# Revit family: Gleitschlitten Typ HV1, o.D., Ø219 - Ø508mm, (h=94-150 mm)
name_source: partatom
category: HLS-Bauteile
units: mm (PartAtom-declared; Revit-internal decimal feet)

## family parameters
Arbeitsebenenbasiert = Ja
Beim Laden mit Abzugskörper schneiden = Nein
Bemaßung runder Anschluss = Durchmesser verwenden
Beschriftungsausrichtung beibehalten = Nein
Gemeinsam genutzt = Ja
Immer vertikal = Nein
Klassifizierung = Keine
Raumberechnungspunkt = Nein
Teiletyp = Normal

## types (13) — shared parameters
Breite Schellenband = 50 mm
Fabrikat = MEFA
Kurztext1 = Gleitschlitten A HV 100-150 50x5
Material = Stahl
Materialname = S235
Mengeneinheit = St
Schalldämmeinlage = ohne Dämmung
Sicherheitsfaktor = 1.54
Stärke Schellenband = 5 mm
Verschluss = Mutter / Verschluss-Schraube
Verschluss-Schraube = M12
Vorgabe-Ansicht = 1219 mm
max. Höhe Unterbau = 150 mm
min. Höhe Unterbau = 100 mm
vpe = 1
zero-valued in all types: Dämmstärke

## per-type parameters (varying)
| type | A (Breite) | Achse Bohrloch | Artikelnummer | Breite Unterbau | EAN | Gewicht | Gewicht pro Bauteil | Kurztext2 | L | L Unterbau | Länge Unterbau | Nennweite DN Rohr | Rohraußendurchmesser | Schellenteil | Stärke Material | TL-Fuß |
| Gleitschlitten HV1, o.D., Ø219mm, h=94mm bis h=150mm | 140 mm  [stored 0.459318 ft] | 90 mm  [stored 0.295276 ft] | 142afa0219 | 256 mm | 4250928462534 | 11.95 kg | 11.95 kg | 219 mm o. Dämm. fsv | 160 mm  [stored 0.524934 ft] | 270 mm  [stored 0.885827 ft] | 270 mm | 200 mm  [stored 0.656168 ft] | 219 mm  [stored 0.718504 ft] | Schellenteil für HV mit RS oD : Schellenteil für 219 | 6 mm  [stored 0.019685 ft] | Gruppe Gleischlitten HV1 Ø219 bis 508 : Gl.0219 |
| Gleitschlitten HV1, o.D., Ø225mm, h=94mm bis h=150mm | 140 mm  [stored 0.459318 ft] | 90 mm  [stored 0.295276 ft] | 142afa0225 | 256 mm | 4250928462541 | 12.12 kg | 12.12 kg | 225 mm o. Dämm. fsv | 160 mm  [stored 0.524934 ft] | 270 mm  [stored 0.885827 ft] | 270 mm | 0 mm  [stored 0 ft] | 225 mm  [stored 0.738189 ft] | Schellenteil für HV mit RS oD : Schellenteil für 225 | 6 mm  [stored 0.019685 ft] | Gruppe Gleischlitten HV1 Ø219 bis 508 : Gl.0225 |
| Gleitschlitten HV1, o.D., Ø273mm, h=94mm bis h=150mm | 172 mm  [stored 0.564304 ft] | 90 mm  [stored 0.295276 ft] | 142afa0273 | 288 mm | 4250928462558 | 12.99 kg | 12.99 kg | 273 mm o. Dämm. fsv | 160 mm  [stored 0.524934 ft] | 270 mm  [stored 0.885827 ft] | 270 mm | 250 mm  [stored 0.82021 ft] | 273 mm  [stored 0.895669 ft] | Schellenteil für HV mit RS oD : Schellenteil für 273 | 6 mm  [stored 0.019685 ft] | Gruppe Gleischlitten HV1 Ø219 bis 508 : Gl.0273 |
| Gleitschlitten HV1, o.D., Ø280mm, h=94mm bis h=150mm | 172 mm  [stored 0.564304 ft] | 90 mm  [stored 0.295276 ft] | 142afa0280 | 288 mm | 4250928462565 | 13.08 kg | 13.08 kg | 280 mm o. Dämm. fsv | 160 mm  [stored 0.524934 ft] | 270 mm  [stored 0.885827 ft] | 270 mm | 0 mm  [stored 0 ft] | 280 mm  [stored 0.918635 ft] | Schellenteil für HV mit RS oD : Schellenteil für 280 | 6 mm  [stored 0.019685 ft] | Gruppe Gleischlitten HV1 Ø219 bis 508 : Gl.0280 |
| Gleitschlitten HV1, o.D., Ø315mm, h=94mm bis h=150mm | 172 mm  [stored 0.564304 ft] | 90 mm  [stored 0.295276 ft] | 142afa0315 | 288 mm | 4250928462572 | 13.43 kg | 13.43 kg | 315 mm o. Dämm. fsv | 160 mm  [stored 0.524934 ft] | 270 mm  [stored 0.885827 ft] | 270 mm | 0 mm  [stored 0 ft] | 315 mm  [stored 1.03346 ft] | Schellenteil für HV mit RS oD : Schellenteil für 315 | 6 mm  [stored 0.019685 ft] | Gruppe Gleischlitten HV1 Ø219 bis 508 : Gl.0315 |
| Gleitschlitten HV1, o.D., Ø324mm, h=94mm bis h=150mm | 172 mm  [stored 0.564304 ft] | 90 mm  [stored 0.295276 ft] | 142afa0324 | 288 mm | 4250928462589 | 13.56 kg | 13.56 kg | 324 mm o. Dämm. fsv | 160 mm  [stored 0.524934 ft] | 270 mm  [stored 0.885827 ft] | 270 mm | 300 mm | 324 mm  [stored 1.06299 ft] | Schellenteil für HV mit RS oD : Schellenteil für 324 | 6 mm  [stored 0.019685 ft] | Gruppe Gleischlitten HV1 Ø219 bis 508 : Gl.0324 |
| Gleitschlitten HV1, o.D., Ø356mm, h=94mm bis h=150mm | 172 mm  [stored 0.564304 ft] | 90 mm  [stored 0.295276 ft] | 142afa0356 | 288 mm | 4250928462596 | 13.87 kg | 13.87 kg | 356 mm o. Dämm. fsv | 160 mm  [stored 0.524934 ft] | 270 mm  [stored 0.885827 ft] | 270 mm | 0 mm  [stored 0 ft] | 356 mm  [stored 1.16798 ft] | Schellenteil für HV mit RS oD : Schellenteil für 356 | 6 mm  [stored 0.019685 ft] | Gruppe Gleischlitten HV1 Ø219 bis 508 : Gl.0356 |
| Gleitschlitten HV1, o.D., Ø400mm, h=94mm bis h=150mm | 225 mm  [stored 0.738189 ft] | 95 mm  [stored 0.31168 ft] | 142afa0400 | 341 mm | 4250928462602 | 17.57 kg | 17.57 kg | 400 mm o. Dämm. fsv | 160 mm  [stored 0.524934 ft] | 270 mm  [stored 0.885827 ft] | 270 mm | 0 mm  [stored 0 ft] | 400 mm  [stored 1.31234 ft] | Schellenteil für HV mit RS oD : Schellenteil für 400 | 8 mm  [stored 0.0262467 ft] | Gruppe Gleischlitten HV1 Ø219 bis 508 : Gl.0400 |
| Gleitschlitten HV1, o.D., Ø406mm, h=94mm bis h=150mm | 225 mm  [stored 0.738189 ft] | 95 mm  [stored 0.31168 ft] | 142afa0406 | 341 mm | 4250928462619 | 17.70 kg | 17.70 kg | 406 mm o. Dämm. fsv | 160 mm  [stored 0.524934 ft] | 270 mm  [stored 0.885827 ft] | 270 mm | 400 mm  [stored 1.31234 ft] | 406 mm  [stored 1.33202 ft] | Schellenteil für HV mit RS oD : Schellenteil für 406 | 8 mm  [stored 0.0262467 ft] | Gruppe Gleischlitten HV1 Ø219 bis 508 : Gl.0406 |
| Gleitschlitten HV1, o.D., Ø450mm, h=94mm bis h=150mm | 225 mm  [stored 0.738189 ft] | 95 mm  [stored 0.31168 ft] | 142afa0450 | 341 mm | 4250928462626 | 18.24 kg | 18.24 kg | 450 mm o. Dämm. fsv | 160 mm  [stored 0.524934 ft] | 270 mm  [stored 0.885827 ft] | 270 mm | 0 mm  [stored 0 ft] | 450 mm  [stored 1.47638 ft] | Schellenteil für HV mit RS oD : Schellenteil für 450 | 8 mm  [stored 0.0262467 ft] | Gruppe Gleischlitten HV1 Ø219 bis 508 : Gl.0450 |
| Gleitschlitten HV1, o.D., Ø457mm, h=94mm bis h=150mm | 225 mm  [stored 0.738189 ft] | 95 mm  [stored 0.31168 ft] | 142afa0457 | 341 mm | 4250928462633 | 18.17 kg | 18.17 kg | 457 mm o. Dämm. fsv | 160 mm  [stored 0.524934 ft] | 270 mm  [stored 0.885827 ft] | 270 mm | 450 mm  [stored 1.47638 ft] | 457 mm  [stored 1.49934 ft] | Schellenteil für HV mit RS oD : Schellenteil für 457 | 8 mm  [stored 0.0262467 ft] | Gruppe Gleischlitten HV1 Ø219 bis 508 : Gl.0457 |
| Gleitschlitten HV1, o.D., Ø500mm, h=94mm bis h=150mm | 254 mm  [stored 0.833333 ft] | 100 mm  [stored 0.328084 ft] | 142afa0500 | 370 mm | 4250928462640 | 24.44 kg | 24.44 kg | 500 mm o. Dämm. fsv | 280 mm  [stored 0.918635 ft] | 390 mm  [stored 1.27953 ft] | 390 mm | 0 mm  [stored 0 ft] | 500 mm  [stored 1.64042 ft] | Schellenteil für HV mit RS oD : Schellenteil für 500 | 8 mm  [stored 0.0262467 ft] | Gruppe Gleischlitten HV1 Ø219 bis 508 : Gl.0500 |
| Gleitschlitten HV1, o.D., Ø508mm, h=94mm bis h=150mm | 254 mm  [stored 0.833333 ft] | 100 mm  [stored 0.328084 ft] | 142afa0508 | 370 mm | 4250928462657 | 24.56 kg | 24.56 kg | 508 mm o. Dämm. fsv | 280 mm  [stored 0.918635 ft] | 390 mm  [stored 1.27953 ft] | 390 mm | 500 mm  [stored 1.64042 ft] | 508 mm | Schellenteil für HV mit RS oD : Schellenteil für 508 | 8 mm  [stored 0.0262467 ft] | Gruppe Gleischlitten HV1 Ø219 bis 508 : Gl.0508 |

note: [stored X ft] marks values corroborated as IEEE doubles in the binary element streams (Revit-internal decimal feet)

## geometry (parser evidence)
native form markers: Sweep x11
no freeform markers — native parametric forms only
